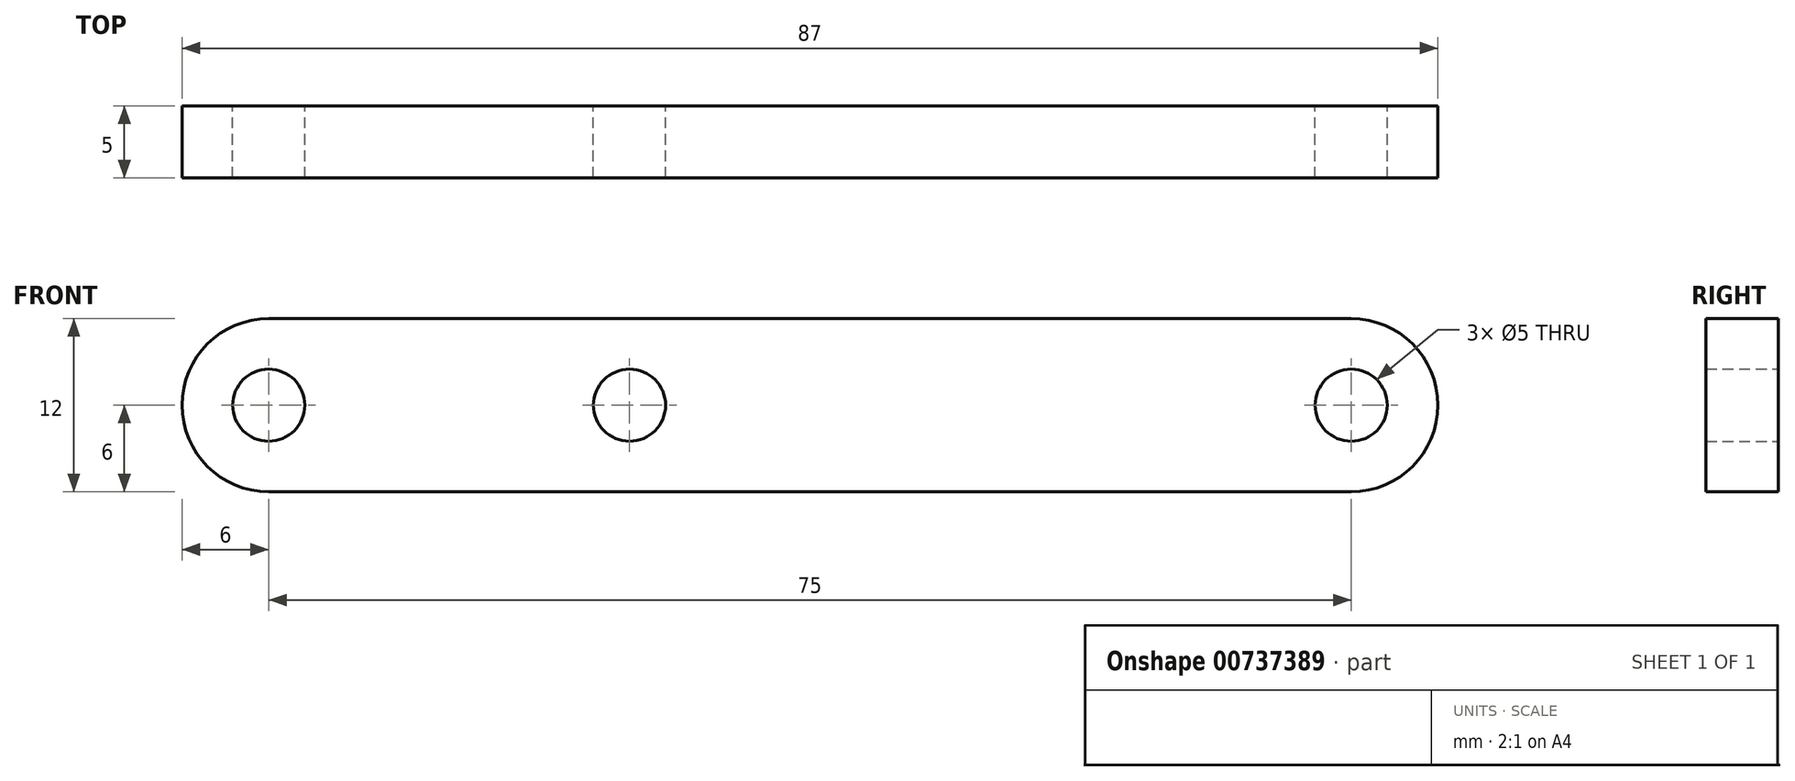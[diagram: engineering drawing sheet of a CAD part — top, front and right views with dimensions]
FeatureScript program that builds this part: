
annotation { "Feature Type Name" : "Feature", "Feature Type Description" : "" }
export const myFeature = defineFeature(function(context is Context, id is Id, definition is map)
    precondition{}
    {
        {
            var Q0;
            Q0=qCreatedBy(makeId("Front.planeOp"),FACE);
            var sketch = newSketch(context, id + "F0", { "sketchPlane" : qUnion([Q0])});
            skLineSegment(sketch, "E0.bottom", {"start": v(0, 0) * mm, "end": v(75, 0) * mm});
            skLineSegment(sketch, "E0.top", {"start": v(0, 12) * mm, "end": v(75, 12) * mm});
            skArc(sketch, "E1", {"start": v(75, 0) * mm, "mid": v(81, 6) * mm, "end": v(75, 12) * mm});
            skArc(sketch, "E2", {"start": v(0, 12) * mm, "mid": v(-6, 6) * mm, "end": v(0, 0) * mm});
            skCircle(sketch, "E3", {"center": v(0, 6) * mm, "radius": 2.5 * mm});
            skCircle(sketch, "E4", {"center": v(75, 6) * mm, "radius": 2.5 * mm});
            skCircle(sketch, "E5", {"center": v(25, 6) * mm, "radius": 2.5 * mm});
            skSolve(sketch);
        }
        {
            var Q0;
            Q0=makeQuery(id+"F0.imprint","IMPRINT",FACE,{"disambiguationData":[TD([[makeQuery(id+"F0.imprint","IMPRINT",EDGE,{"derivedFrom":sQuery(id+"F0.wireOp",EDGE,"E0.bottom")}),1.0]])]});
            var Q1;
            Q1=makeQuery(id+"F0.imprint","IMPRINT",FACE,{"disambiguationData":[TD([[makeQuery(id+"F0.imprint","IMPRINT",EDGE,{"derivedFrom":sQuery(id+"F0.wireOp",EDGE,"OiZRVR2j-fgGC-Y1c5-xTuJ-MU726yC0vpi6")}),1.0]])]});
            var Q2;
            Q2=makeQuery(id+"F0.imprint","IMPRINT",FACE,{"disambiguationData":[TD([[makeQuery(id+"F0.imprint","IMPRINT",EDGE,{"derivedFrom":sQuery(id+"F0.wireOp",EDGE,"OVGhL1fR-kpwL-Q1Y9-nKem-xCdm6wDIFtNx")}),1.0]])]});
            extrude(context, id + "F1", {"entities" : qUnion([Q0, Q1, Q2]), "depth" : 5 * mm, "offsetDistance" : 25 * mm});
        }
    });
